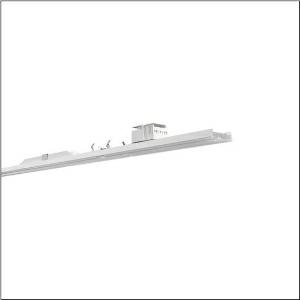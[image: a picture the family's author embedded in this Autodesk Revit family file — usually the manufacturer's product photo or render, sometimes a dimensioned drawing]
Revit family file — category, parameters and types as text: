
# Revit family: licross_r__11_recessed_mo_51tl11dn49xfd_8b8a
name_source: partatom
category: Lighting Fixtures
units: mm (PartAtom-declared; Revit-internal decimal feet)

## family parameters
Cut with Voids When Loaded = No
Host = Face
Light Source = No
Part Type = Normal
Room Calculation Point = No
Round Connector Dimension = Use Diameter
Shared = No

## types (1)
- --- (1 x LED, 1440 lm, 9.8 W, 4000K)
    Apparent Load = 10 VA
    CIE Flux Codes = 89 96 99 100 100
    Color Rendering = 80
    Color Temperature = 4000K
    Default Elevation = 1800 mm
    Description = Licross® 11 Recessed MOluminaire insert, length: 1.500mm, width: 66mm, height: 67mm, LED rated luminous flux: 9.030lm, light colour: 840, control gear: DALI 2, control gear: ECG DALI, with plug, 6-pole, with phase selection, mains connection: 220..240V, AC/DC, 0/50..60Hz, without changeover relay, for emergency light function, for central battery installations according to DIN EN 60598-2-22, halogen-free wiring, primary optical cover: cover, of PMMA, light emission: direct distribution, protection rating (complete): IP40, insulation class (complete): insulation class I (protective earthing), certification: CE, ENEC, VDE, protection symbol: D if used in an environment without relevant dust loads with corresponding accessories, permissible ambient temperature for indoor applications: -25..+40°C, standard: EN 60598-2-22, reducing of maximum allowable ambient temperature of 5°C with ceiling mounting, corresponds to IFS (International Featured Standards) requirements for safety and quality in the food industry, packaging unit: 1 piece
    Height = 58 mm
    Lamp = 1 x LED
    Lamp Light Flux = 1440 lm
    Lamp Power = 9.8 W
    Lamp count = 1
    Length = 1500 mm
    Luminous efficacy = 147 lm/W
    Manufacturer = Siteco
    ModVariant = No
    Model = 51TL11DN49XFD
    Mounting Place = Ceiling
    Mounting Type = Pendant
    Number of Poles = 1
    OnlyDefault = Yes
    Power Factor = 1
    Product Name = Licross® 11 Recessed MO
    Product group = luminaire insert
    ProductGroupID = 902
    Protection Class = Protection class I
    Protection Degree = IP 40
    RLX_Detail_Level = 1
    RlxData = <blob elided: 22641 chars, md5=226eb505>
    Socket = socket
    Standby Power = 0 W
    System Light Flux = 1440 lm
    System Power = 10 W
    Type Comments = : DC mode (central or group accumulator) initial emergency light level
    Type Image = l_1266722.jpg
    URL = http://relux.com
    VarID = @adj_134049
    Voltage = 0 V
    Weight = 0.00 kg
    Width = 66 mm

## geometry (parser evidence)
native form markers: Blend x4, Sweep x11
no freeform markers — native parametric forms only
